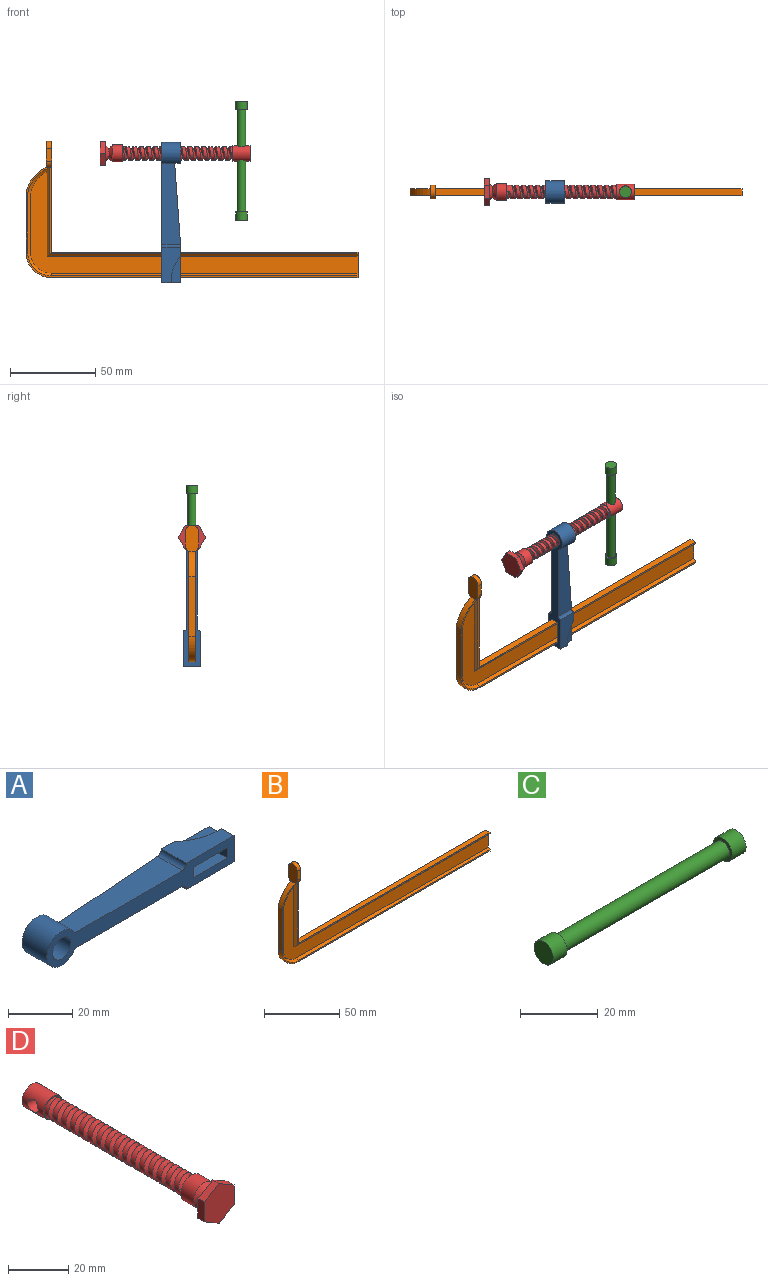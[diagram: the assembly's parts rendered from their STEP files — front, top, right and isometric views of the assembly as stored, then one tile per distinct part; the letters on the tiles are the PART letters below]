
ASSEMBLY  parts=4 mates=4
PART A: 20 faces, bbox 82.5x11x13 mm
  f0: plane 47.54x11mm, normal (0,0,1), area 440.9mm2, adj f4,f13,f15,f19
  f1: plane 13x12.27mm, normal (0,1,0), area 79.5mm2, adj f4,f5,f18
  f2: plane 11x10mm, normal (1,0,0), area 99mm2, adj f3,f6,f8,f15,f16,f17
  f3: plane 21x11mm, normal (0,0,1), area 170.6mm2, adj f2,f6,f13,f15,f16
  f4: cylinder r=6.5mm len=13mm, axis (0,1,0), area 380.6mm2, adj f0,f1,f7,f15,f18
  f5: cylinder r=4mm len=11mm, axis (0,1,0), area 276.5mm2, adj f1,f15
  f6: plane 22.69x10mm, normal (0,1,0), area 131.2mm2, adj f2,f3,f7,f8,f9,f10,f11,f12
  f7: plane 47.69x11mm, normal (0,0,-1), area 442.5mm2, adj f4,f6,f14,f15,f19
  f8: plane 21x11mm, normal (0,0,-1), area 231mm2, adj f2,f6,f14,f15
  f9: plane 11x4mm, normal (-1,0,0), area 44mm2, adj f6,f10,f12,f15
  f10: plane 15x11mm, normal (0,0,1), area 165mm2, adj f6,f9,f11,f15
  f11: plane 11x4mm, normal (1,0,0), area 44mm2, adj f6,f10,f12,f15
  f12: plane 15x11mm, normal (0,0,-1), area 165mm2, adj f6,f9,f11,f15
  f13: cylinder r=2.03mm len=11mm, axis (0,-1,0), area 31.3mm2, adj f0,f3,f6,f15
  f14: cylinder r=2.07mm len=11mm, axis (0,-1,0), area 29.9mm2, adj f6,f7,f8,f15
  f15: plane 82.5x13mm, normal (0,-1,0), area 526.5mm2, adj f0,f2,f3,f4,f5,f7,f8,f9
  f16: cylinder r=20.45mm len=15.29mm, axis (0,0,1), area 33.4mm2, adj f2,f3,f6,f17
  f17: plane 15.29x5.54mm, normal (0,0,1), area 60.4mm2, adj f2,f6,f16
  f18: plane 6x3.45mm, normal (1,0,0), area 20.7mm2, adj f1,f4,f19
  f19: plane 47.54x6mm, normal (-0.07,1,0), area 286mm2, adj f0,f6,f7,f18
PART B: 22 faces, bbox 195x8x80 mm
  f0: plane 195x65mm, normal (0,1,0), area 3565.3mm2, adj f2,f3,f4,f5,f6,f7,f9,f13
  f1: plane 195x65mm, normal (0,-1,0), area 489.2mm2, adj f2,f3,f4,f5,f6,f7,f9,f15
  f2: plane 15x4mm, normal (1,0,0), area 42.7mm2, adj f0,f1,f6,f7,f10,f16,f21
  f3: plane 65x8mm, normal (1,0,0), area 309.1mm2, adj f0,f1,f7,f11,f12,f13,f14,f15
  f4: plane 35x4mm, normal (-1,0,0), area 140mm2, adj f0,f1,f5,f9
  f5: cylinder r=15mm len=15mm, axis (0,1,0), area 94.2mm2, adj f0,f1,f4,f6
  f6: plane 180x4mm, normal (0,0,-1), area 720mm2, adj f0,f1,f2,f5
  f7: plane 180x4mm, normal (0,0,1), area 720mm2, adj f0,f1,f2,f3
  f8: plane 15x8mm, normal (-1,0,0), area 109.1mm2, adj f9,f11,f12,f13,f14,f15
  f9: cylinder r=22mm len=15mm, axis (0,-1,0), area 79.5mm2, adj f0,f1,f4,f8
  f10: plane 192.5x59.96mm, normal (0,-1,0), area 2346.5mm2, adj f2,f16,f17,f18,f19,f20,f21
  f11: plane 7.54x3mm, normal (0,-1,0), area 22.6mm2, adj f3,f8,f14,f15
  f12: plane 7.54x3mm, normal (0,1,0), area 22.6mm2, adj f3,f8,f13,f14
  f13: cylinder r=4mm len=3.46mm, axis (1,0,0), area 12.6mm2, adj f0,f3,f8,f12
  f14: cylinder r=4mm len=8mm, axis (-1,0,0), area 37.7mm2, adj f3,f8,f11,f12
  f15: cylinder r=4mm len=3.46mm, axis (-1,0,0), area 12.6mm2, adj f1,f3,f8,f11
  f16: plane 180x1.5mm, normal (0,-0.71,0.71), area 381.8mm2, adj f1,f2,f10,f17
  f17: cone r=12.5mm half-angle=45deg, axis (0,-1,0), area 44.2mm2, adj f1,f10,f16,f18
  f18: plane 34.89x1.5mm, normal (0.71,-0.71,0), area 73.8mm2, adj f1,f10,f17,f19
  f19: cone r=19.5mm half-angle=45deg, axis (0,-1,0), area 39.6mm2, adj f1,f10,f18,f20
  f20: plane 52.27x1.5mm, normal (-0.71,-0.71,0), area 106.9mm2, adj f1,f10,f19,f21
  f21: plane 182.5x1.5mm, normal (0,-0.71,-0.71), area 385.5mm2, adj f1,f2,f10,f20
PART C: 7 faces, bbox 70x7x7 mm
  f0: cylinder r=3.5mm len=7mm, axis (-1,0,0), area 110mm2, adj f1,f2
  f1: plane 7x7mm, normal (1,0,0), area 18.8mm2, adj f0,f3
  f2: plane 7x7mm, normal (-1,0,0), area 38.5mm2, adj f0
  f3: cylinder r=2.5mm len=60mm, axis (-1,0,0), area 942.5mm2, adj f1,f6
  f4: cylinder r=3.5mm len=7mm, axis (-1,0,0), area 110mm2, adj f5,f6
  f5: plane 7x7mm, normal (1,0,0), area 38.5mm2, adj f4
  f6: plane 7x7mm, normal (-1,0,0), area 18.8mm2, adj f3,f4
PART D: 22 faces, bbox 13.9x88x16.1 mm
  f0: cylinder r=4mm len=65mm, axis (0,1,0), area 653.9mm2, adj f3,f15,f18,f19,f21
  f1: cylinder r=4.5mm len=10mm, axis (0,-1,0), area 241mm2, adj f14,f15,f16
  f2: cylinder r=5mm len=10mm, axis (0,1,0), area 188.5mm2, adj f3,f4
  f3: plane 10x10mm, normal (0,1,0), area 28.3mm2, adj f0,f2
  f4: cone r=3mm half-angle=45deg, axis (0,1,0), area 71.1mm2, adj f2,f5
  f5: cone r=5mm half-angle=45deg, axis (0,-1,0), area 71.1mm2, adj f4,f13
  f6: plane 8.04x3mm, normal (-1,0,0), area 24.1mm2, adj f7,f11,f12,f13
  f7: plane 6.96x4.02mm, normal (-0.5,0,-0.87), area 24.1mm2, adj f6,f8,f12,f13
  f8: plane 6.96x4.02mm, normal (0.5,0,-0.87), area 24.1mm2, adj f7,f9,f12,f13
  f9: plane 8.04x3mm, normal (1,0,0), area 24.1mm2, adj f8,f10,f12,f13
  f10: plane 6.96x4.02mm, normal (0.5,0,0.87), area 24.1mm2, adj f9,f11,f12,f13
  f11: plane 6.96x4.02mm, normal (-0.5,0,0.87), area 24.1mm2, adj f6,f10,f12,f13
  f12: plane 16.08x13.93mm, normal (0,-1,0), area 168mm2, adj f6,f7,f8,f9,f10,f11
  f13: plane 16.08x13.93mm, normal (0,1,0), area 89.5mm2, adj f5,f6,f7,f8,f9,f10,f11
  f14: plane 9x9mm, normal (0,1,0), area 63.6mm2, adj f1
  f15: plane 9x9mm, normal (0,-1,0), area 13.4mm2, adj f0,f1,f20
  f16: cylinder r=2.52mm len=9mm, axis (1,0,0), area 130.6mm2, adj f1
  f17: plane 2x1.73mm, normal (0,0,-1), area 1.7mm2, adj f19,f20,f21
  f18: plane 2x1.73mm, normal (0,0,1), area 1.7mm2, adj f0,f19,f21
  f19: bspline ~66x9.24mm, area 642.4mm2, adj f0,f17,f18,f21
  f20: cylinder r=4mm len=7.99mm, axis (0,-1,0), area 12.4mm2, adj f15,f17,f21
  f21: bspline ~66x9.24mm, area 642.4mm2, adj f0,f17,f18,f19,f20
PLACE A rot(axis=(0.58,0.58,-0.58),120deg) t=(-18.05,32.97,9.47)mm
PLACE B t=(-93.81,34.97,-48.53)mm fixed
PLACE C rot(axis=(0,-1,0),90deg) t=(17.77,32.97,-29.89)mm
PLACE D rot(axis=(0.58,0.58,-0.58),120deg) t=(12.77,32.97,9.47)mm
MATE slider C.f0 <-> D.f16  axis (0,0,-1) through (17.77,32.97,5.11)mm
MATE slider D.f0 <-> A.f4  axis (1,0,0) through (-52.23,32.97,9.47)mm
MATE slider A.f4 <-> D.f2  axis (1,0,0) through (-23.55,32.97,9.47)mm
MATE slider A.f6 <-> B.f2  axis (1,0,0) through (-18.05,34.97,-48.53)mm
